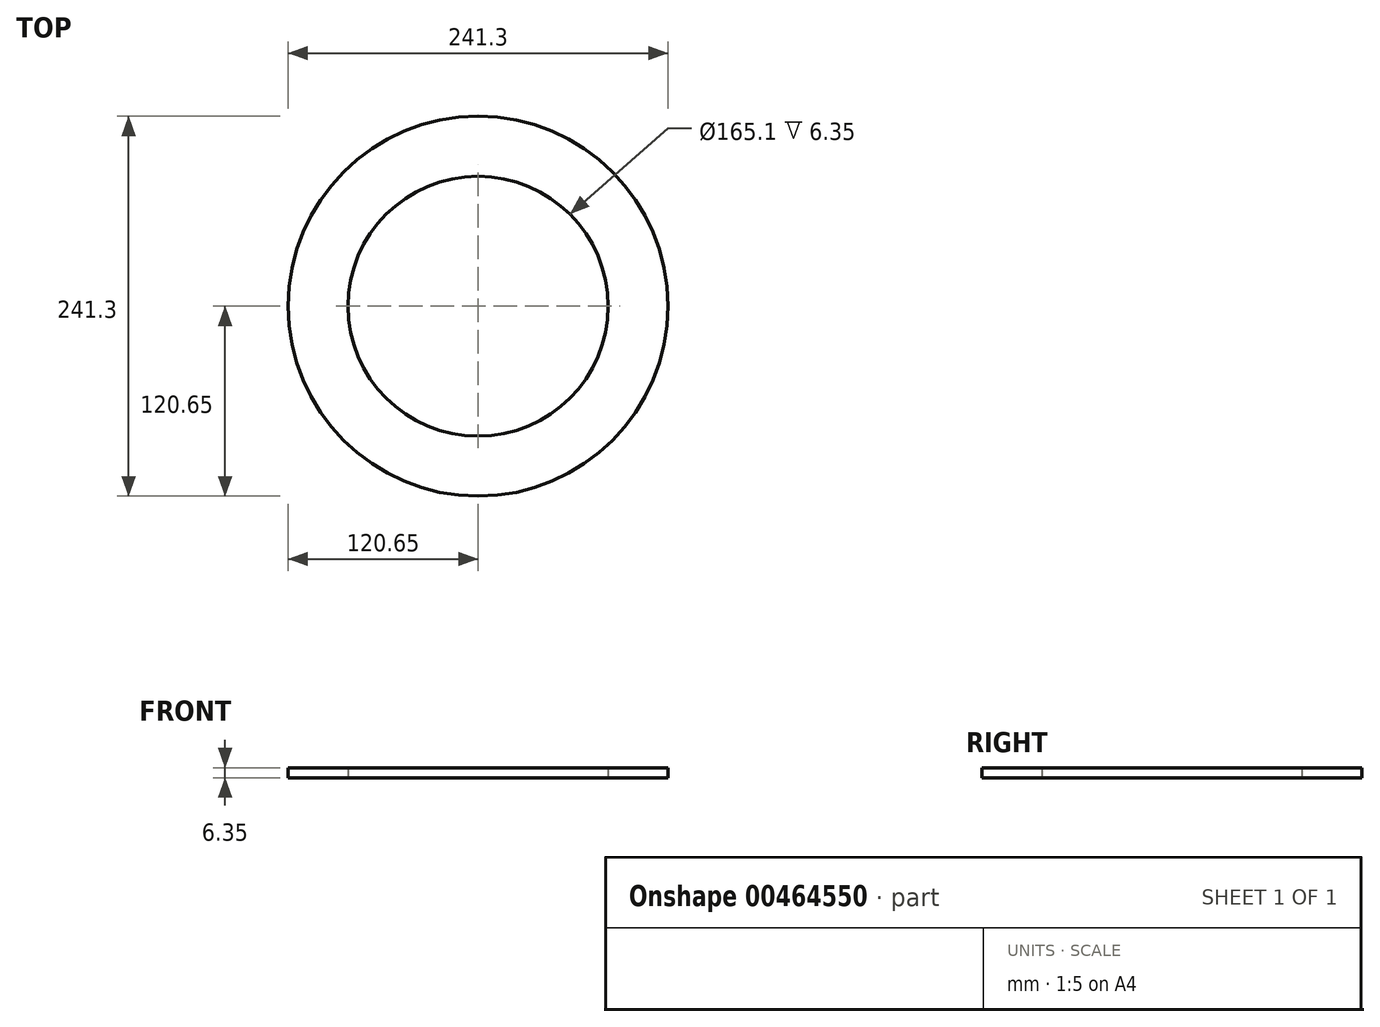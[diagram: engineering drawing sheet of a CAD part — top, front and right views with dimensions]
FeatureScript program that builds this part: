
annotation { "Feature Type Name" : "Feature", "Feature Type Description" : "" }
export const myFeature = defineFeature(function(context is Context, id is Id, definition is map)
    precondition{}
    {
        {
            var Q0;
            Q0=qCreatedBy(makeId("Top.planeOp"),FACE);
            var sketch = newSketch(context, id + "F0", { "sketchPlane" : qUnion([Q0])});
            skCircle(sketch, "E0", {"center": v(0, 0) * mm, "radius": 120.65 * mm});
            skCircle(sketch, "E1", {"center": v(0, 0) * mm, "radius": 82.55 * mm});
            skSolve(sketch);
        }
        {
            var Q0;
            Q0=makeQuery(id+"F0.imprint","IMPRINT",FACE,{"disambiguationData":[TD([[makeQuery(id+"F0.imprint","IMPRINT",EDGE,{"derivedFrom":sQuery(id+"F0.wireOp",EDGE,"E0")}),1.0]])]});
            extrude(context, id + "F1", {"entities" : qUnion([Q0]), "depth" : 6.35 * mm});
        }
    });
